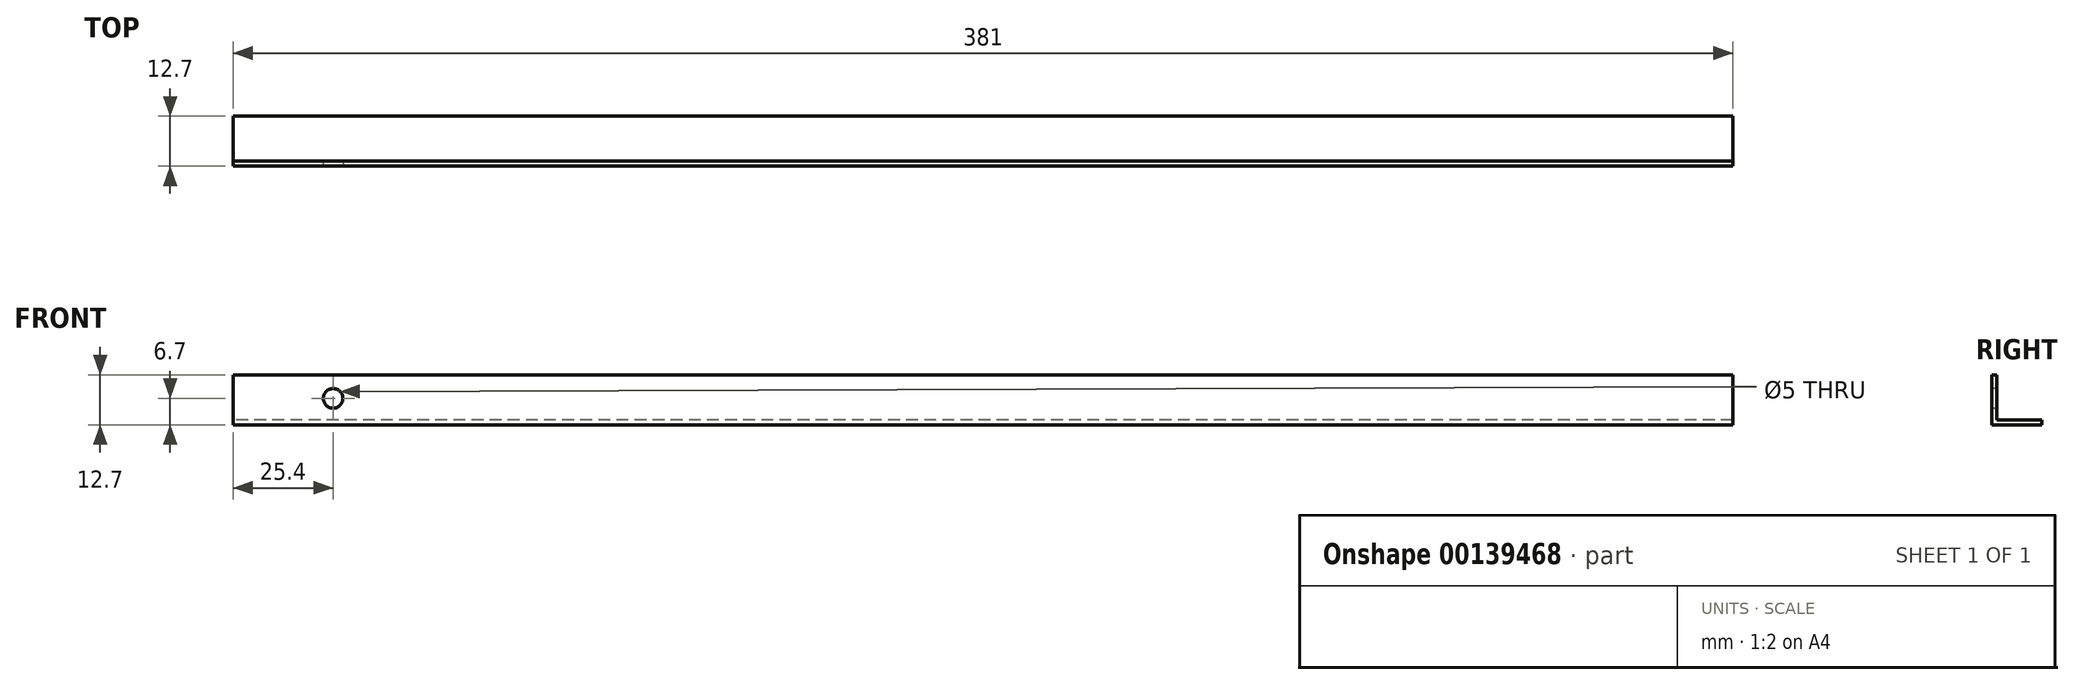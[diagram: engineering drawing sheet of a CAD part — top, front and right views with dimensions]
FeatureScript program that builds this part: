
annotation { "Feature Type Name" : "Feature", "Feature Type Description" : "" }
export const myFeature = defineFeature(function(context is Context, id is Id, definition is map)
    precondition{}
    {
        {
            var Q0;
            Q0=qCreatedBy(makeId("Right.planeOp"),FACE);
            var sketch = newSketch(context, id + "F0", { "sketchPlane" : qUnion([Q0])});
            skLineSegment(sketch, "E0", {"start": v(0, 0) * mm, "end": v(12.7, 0) * mm});
            skLineSegment(sketch, "E1", {"start": v(12.7, 0) * mm, "end": v(12.7, 1.27) * mm});
            skLineSegment(sketch, "E2", {"start": v(12.7, 1.27) * mm, "end": v(1.27, 1.27) * mm});
            skLineSegment(sketch, "E3", {"start": v(1.27, 1.27) * mm, "end": v(1.27, 12.7) * mm});
            skLineSegment(sketch, "E4", {"start": v(1.27, 12.7) * mm, "end": v(0, 12.7) * mm});
            skLineSegment(sketch, "E5", {"start": v(0, 12.7) * mm, "end": v(0, 0) * mm});
            skSolve(sketch);
        }
        {
            var Q0;
            Q0=makeQuery(id+"F0.imprint","IMPRINT",FACE,{"disambiguationData":[TD([[makeQuery(id+"F0.imprint","IMPRINT",EDGE,{"derivedFrom":sQuery(id+"F0.wireOp",EDGE,"E0")}),1.0]])]});
            extrude(context, id + "F1", {"entities" : qUnion([Q0]), "depth" : 381 * mm});
        }
        {
            var Q0;
            Q0=makeQuery(id+"F1.opExtrude","SWEPT_FACE",FACE,{"disambiguationData":[OSD([sQuery(id+"F0.wireOp",EDGE,"E5")])]});
            var sketch = newSketch(context, id + "F2", { "sketchPlane" : qUnion([Q0])});
            skLineSegment(sketch, "E6", {"start": v(0, 12.7) * mm, "end": v(25.4, 12.7) * mm, "construction": true});
            skLineSegment(sketch, "E7", {"start": v(25.4, 12.7) * mm, "end": v(25.4, 6.7) * mm, "construction": true});
            skCircle(sketch, "E8", {"center": v(25.4, 6.7) * mm, "radius": 2.5 * mm});
            skCircle(sketch, "E9", {"center": v(25.4, 6.7) * mm, "radius": 8 * mm, "construction": true});
            skSolve(sketch);
        }
        {
            var Q0;
            Q0=makeQuery(id+"F2.imprint","IMPRINT",FACE,{"disambiguationData":[TD([[makeQuery(id+"F2.imprint","IMPRINT",EDGE,{"derivedFrom":sQuery(id+"F2.wireOp",EDGE,"E8")}),1.0]])]});
            extrude(context, id + "F3", {"entities" : qUnion([Q0]), "operationType" : NewBodyOperationType.REMOVE, "oppositeDirection" : true, "depth" : 25.4 * mm});
        }
    });
